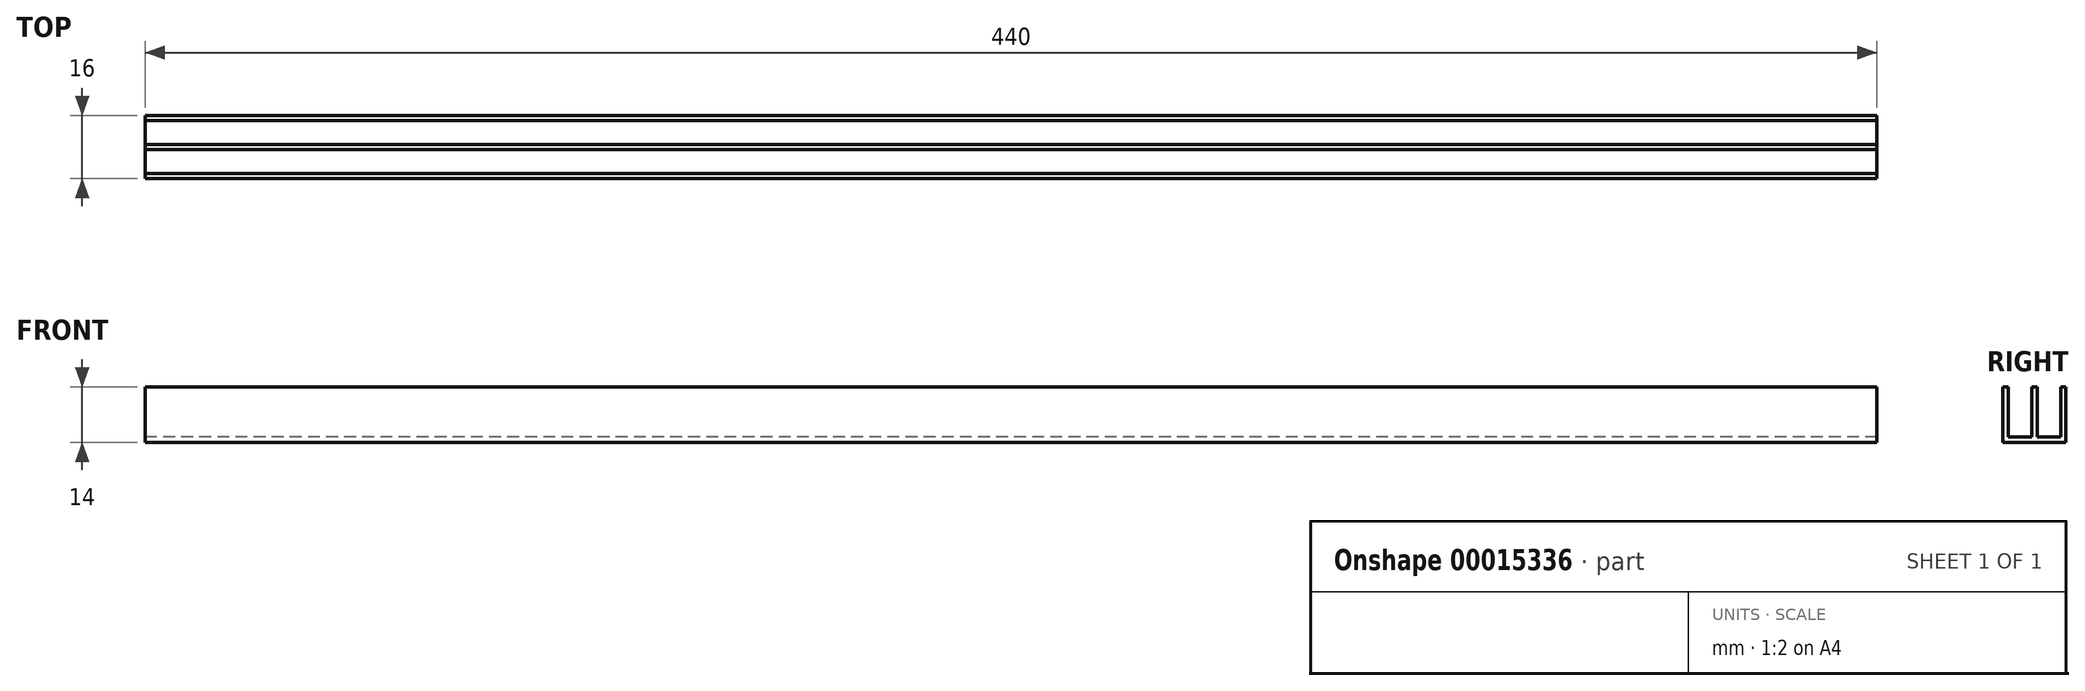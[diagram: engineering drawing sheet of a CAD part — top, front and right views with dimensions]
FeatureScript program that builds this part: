
annotation { "Feature Type Name" : "Feature", "Feature Type Description" : "" }
export const myFeature = defineFeature(function(context is Context, id is Id, definition is map)
    precondition{}
    {
        {
            var Q0;
            Q0=qCreatedBy(makeId("Right.planeOp"),FACE);
            var sketch = newSketch(context, id + "F0", { "sketchPlane" : qUnion([Q0])});
            skLineSegment(sketch, "E0.top", {"start": v(-8, 0) * mm, "end": v(8, 0) * mm});
            skLineSegment(sketch, "E0.left", {"start": v(-8, 14) * mm, "end": v(-8, 0) * mm});
            skLineSegment(sketch, "E0.right", {"start": v(8, 14) * mm, "end": v(8, 0) * mm});
            skLineSegment(sketch, "E1", {"start": v(-8, 14) * mm, "end": v(-6.7, 14) * mm});
            skLineSegment(sketch, "E2", {"start": v(-6.7, 14) * mm, "end": v(-6.7, 1.3) * mm});
            skLineSegment(sketch, "E3", {"start": v(-6.7, 1.3) * mm, "end": v(-0.65, 1.3) * mm});
            skLineSegment(sketch, "E4", {"start": v(-0.65, 1.3) * mm, "end": v(-0.65, 14) * mm});
            skLineSegment(sketch, "E5", {"start": v(-0.65, 14) * mm, "end": v(0.65, 14) * mm});
            skLineSegment(sketch, "E6", {"start": v(0.65, 14) * mm, "end": v(0.65, 1.3) * mm});
            skLineSegment(sketch, "E7", {"start": v(0.65, 1.3) * mm, "end": v(6.7, 1.3) * mm});
            skLineSegment(sketch, "E8", {"start": v(6.7, 1.3) * mm, "end": v(6.7, 14) * mm});
            skLineSegment(sketch, "E9", {"start": v(6.7, 14) * mm, "end": v(8, 14) * mm});
            skSolve(sketch);
        }
        {
            var Q0;
            Q0=makeQuery(id+"F0.imprint","IMPRINT",FACE,{"disambiguationData":[TD([[makeQuery(id+"F0.imprint","IMPRINT",EDGE,{"derivedFrom":sQuery(id+"F0.wireOp",EDGE,"E0.top")}),1.0]])]});
            extrude(context, id + "F1", {"entities" : qUnion([Q0]), "depth" : 220 * mm, "hasSecondDirection" : true, "secondDirectionOppositeDirection" : true, "secondDirectionDepth" : 220 * mm});
        }
    });
